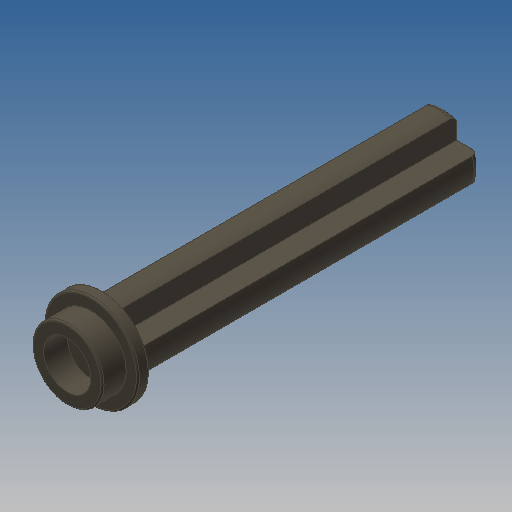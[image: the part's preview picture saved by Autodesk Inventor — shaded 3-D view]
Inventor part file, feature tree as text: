
AUTODESK INVENTOR PART (.ipt)
format: ipt  version: 2022.2 (Build 262287000, 287)  size: 403,968 bytes
history: native  units: in
note: dims shown in document units (in); Inventor stores cm internally (conversion verified against a paired STEP export)
features: sketch x4, extrude x3, other x1, fillet x1
ambient origin geometry x8: Origin, YZ Plane, XZ Plane, XY Plane, X Axis, Y Axis, Z Axis, Center Point
bodies: Solid1 (feature_tree)
feature tree (9):
  extrude  "Extrusion1"  Depth=0.063in
  extrude  "Extrusion2"  TaperAngle=0.0deg  [1 undecoded]
  extrude  "Extrusion3"  Depth=0.0315in
  other  "LEGO_SM:1"
  fillet  "Fillet1"  Radius=0.0315in
  sketch  "Sketch1"  dims[d0=0.189in d1=0.063in]
  sketch  "Sketch2"  dims[d2=0.9134in d3=0.0in]
  sketch  "Sketch3"  dims[d4=0.0157in d7=0.252in d8=0.0315in d9=0.0in]
  sketch  "Sketch4"  dims[d10=0.189in d11=0.126in d12=0.063in d13=0.0in d14=0.0039in d15=0.0in d16=0.0in d17=0.0in d18=0.0055in d19=0.0513in d20=0.0197in d21=0.0245in d22=0.0055in d23=0.0097in d24=0.0197in d25=0.0245in d26=0.0197in d27=0.0111in d28=0.0124in d29=0.0245in d30=0.5428in]
note: 1 required parameter value undecoded (feature->parameter linkage not recoverable at this tier; creation-order binding heuristic only, values carry confidence <= 0.55)
